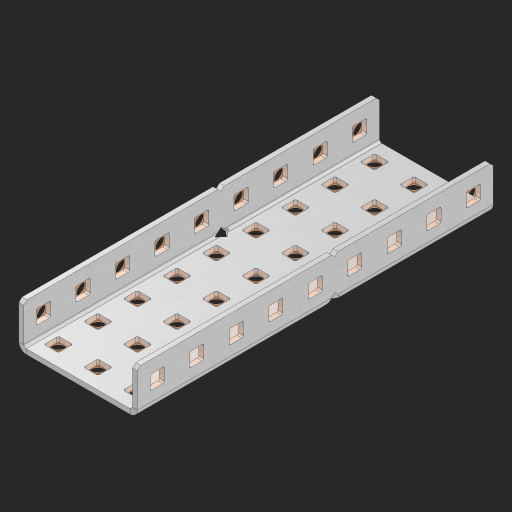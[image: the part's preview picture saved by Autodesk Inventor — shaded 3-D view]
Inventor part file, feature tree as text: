
AUTODESK INVENTOR PART (.ipt)
format: ipt  version: 2023 (Build 270158000, 158)  size: 859,648 bytes
history: native  units: in
note: dims shown in document units (in); Inventor stores cm internally (conversion verified against a paired STEP export)
features: other x50, extrude x44, sheet_metal_op x10, sketch x8, mirror x1, pattern_linear x1, chamfer x1
ambient origin geometry x8: Origin, YZ Plane, XZ Plane, XY Plane, X Axis, Y Axis, Z Axis, Center Point
bodies: Solid1 (feature_tree), Body (feature_tree)
feature tree (115):
  other  "Flange Pattern Plane"
  sheet_metal_op  "Flange Pattern"
  sheet_metal_op  "Body Pattern"
  other  "Arc Length"
  mirror  "Notch Mirror"
  pattern_linear  "Notch Pattern"  Spacing1=0.25in  [1 undecoded]
  chamfer  "End Chamfer"
  extrude  "Half Cut"  Depth=0.0625in
  sketch  "Sketch1"  dims[d0=1.5in]
  other  "Plate1"
  sketch  "Sketch2"  dims[d1=4.5in]
  other  "Plate2"
  sheet_metal_op  "Bend1"
  sheet_metal_op  "Corner1"
  sketch  "Sketch3"  dims[d2=0.0625in]
  other  "Flange Pattern Sketch"
  sketch  "Sketch7"  dims[d3=0.0625in]
  other  "Srf1"
  other  "Srf2"
  sketch  "Sketch8"  dims[d4=0.0312in]
  sketch  "Sketch9"  dims[d5=0.125in]
  other  "Srf91"
  sheet_metal_op  "Body Pattern Sketch"
  other  "Srf92"
  sketch  "Sketch13"  dims[d6=0.0625in]
  sketch  "Sketch14"  dims[d7=0.5in d8=90.0deg d9=0.0312in d10=0.25in d11=0.0625in d12=0.0625in d16=0.182in d17=0.02in d18=0.0625in d19=0.0in d20=0.25in d21=0.25in d46=0.172in d47=1.0in d48=0.0in d49=0.182in d50=0.02in d51=0.25in d52=0.25in d53=0.0625in d54=0.0in d55=0.172in d56=1.0in d57=0.0in d60=3.5433in d62=0.5in d63=1.1811in d65=0.5in d85=0.1473in d86=0.1782in d88=0.04in d89=0.0625in d90=0.0in d91=0.04in d92=0.0491in d95=2.5in d96=0.04in d97=0.25in d98=45.0deg d101=0.0in d102=2.497in d131=1.5in d132=3.5433in d134=0.5in d139=0.5in]
  other  "Srf856"
  other  "Srf1310"
  other  "Srf1311"
  other  "Srf1312"
  other  "Srf1376"
  other  "Srf1377"
  other  "Srf1728"
  other  "Srf1755"
  other  "Srf1878"
  other  "Srf1879"
  other  "Srf1880"
  other  "Srf1881"
  other  "Srf1882"
  other  "Srf1883"
  other  "Srf1884"
  other  "Srf1885"
  other  "Srf1886"
  other  "Srf1887"
  other  "Srf1888"
  other  "Srf1889"
  other  "Srf1942"
  other  "Srf1943"
  other  "Srf1944"
  other  "Srf1945"
  other  "Srf1946"
  other  "Srf1947"
  other  "Srf1948"
  other  "Srf1949"
  other  "Srf1950"
  other  "Srf1951"
  other  "Srf1952"
  other  "Srf1953"
  other  "Srf1954"
  other  "Srf1955"
  other  "Srf1956"
  other  "Srf1957"
  other  "Srf1958"
  other  "Srf1959"
  other  "Srf1960"
  other  "Srf1961"
  other  "Srf1962"
  sheet_metal_op  "Flange Stamp"
  sheet_metal_op  "Flange Circle"
  sheet_metal_op  "Body Stamp"
  sheet_metal_op  "Body Circle"
  sheet_metal_op  "Notch"
  extrude  "ExtrusionSrf2"  Depth=0.0625in
  extrude  "ExtrusionSrf92"  Depth=1.5in
  extrude  "ExtrusionSrf856"  Depth=0.02in
  extrude  "ExtrusionSrf1310"  Depth=0.0625in
  extrude  "ExtrusionSrf1311"  TaperAngle=0.0deg  [1 undecoded]
  extrude  "ExtrusionSrf1312"  Depth=0.25in
  extrude  "ExtrusionSrf1376"  Depth=0.25in
  extrude  "ExtrusionSrf1377"  Depth=1.5in
  extrude  "ExtrusionSrf1728"  Depth=1.5in TaperAngle=0.0deg
  extrude  "ExtrusionSrf1755"  Depth=1.5in
  extrude  "ExtrusionSrf1878"  Depth=0.02in
  extrude  "ExtrusionSrf1879"  Depth=0.25in
  extrude  "ExtrusionSrf1880"  Depth=0.25in
  extrude  "ExtrusionSrf1881"  Depth=0.0625in
  extrude  "ExtrusionSrf1882"  TaperAngle=0.0deg  [1 undecoded]
  extrude  "ExtrusionSrf1883"  Depth=1.5in
  extrude  "ExtrusionSrf1884"  Depth=1.5in TaperAngle=0.0deg
  extrude  "ExtrusionSrf1885"  Depth=1.5in
  extrude  "ExtrusionSrf1886"  Depth=1.5in
  extrude  "ExtrusionSrf1887"  Depth=1.5in
  extrude  "ExtrusionSrf1888"  Depth=1.5in
  extrude  "ExtrusionSrf1889"  Depth=1.5in
  extrude  "ExtrusionSrf1942"  Depth=0.0625in
  extrude  "ExtrusionSrf1943"  TaperAngle=0.0deg  [1 undecoded]
  extrude  "ExtrusionSrf1944"  Depth=1.5in
  extrude  "ExtrusionSrf1945"  Depth=1.5in
  extrude  "ExtrusionSrf1946"  Depth=1.5in
  extrude  "ExtrusionSrf1947"  Depth=0.25in TaperAngle=45.0deg
  extrude  "ExtrusionSrf1948"  TaperAngle=0.0deg  [1 undecoded]
  extrude  "ExtrusionSrf1949"  Depth=1.5in
  extrude  "ExtrusionSrf1950"  Depth=1.5in
  extrude  "ExtrusionSrf1951"  Depth=1.5in
  extrude  "ExtrusionSrf1952"  Depth=1.5in
  extrude  "ExtrusionSrf1953"  Depth=1.5in
  extrude  "ExtrusionSrf1954"  [1 undecoded]
  extrude  "ExtrusionSrf1955"  [1 undecoded]
  extrude  "ExtrusionSrf1956"  [1 undecoded]
  extrude  "ExtrusionSrf1957"  [1 undecoded]
  extrude  "ExtrusionSrf1958"  [1 undecoded]
  extrude  "ExtrusionSrf1959"  [1 undecoded]
  extrude  "ExtrusionSrf1960"  [1 undecoded]
  extrude  "ExtrusionSrf1961"  [1 undecoded]
  extrude  "ExtrusionSrf1962"  [1 undecoded]
note: 14 required parameter values undecoded (feature->parameter linkage not recoverable at this tier; creation-order binding heuristic only, values carry confidence <= 0.55)
